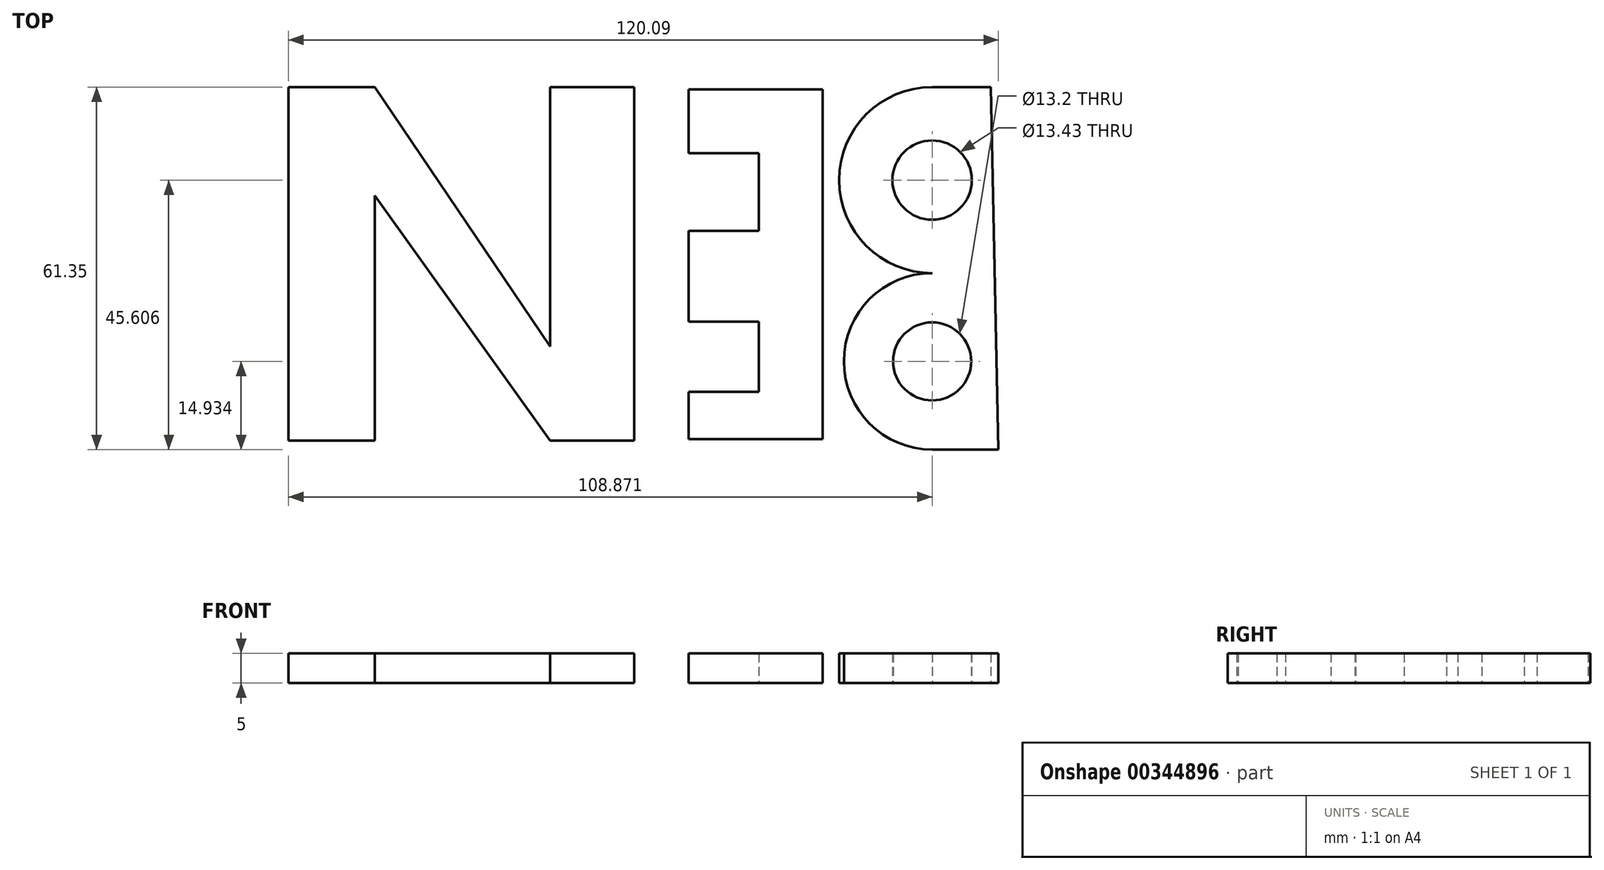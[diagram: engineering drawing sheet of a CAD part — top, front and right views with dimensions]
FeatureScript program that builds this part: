
annotation { "Feature Type Name" : "Feature", "Feature Type Description" : "" }
export const myFeature = defineFeature(function(context is Context, id is Id, definition is map)
    precondition{}
    {
        {
            var Q0;
            Q0=qCreatedBy(makeId("Top.planeOp"),FACE);
            var sketch = newSketch(context, id + "F0", { "sketchPlane" : qUnion([Q0])});
            skArc(sketch, "E0", {"start": v(-12.54, 27.73) * mm, "mid": v(-28.28, 11.99) * mm, "end": v(-12.54, -3.76) * mm});
            skArc(sketch, "E1", {"start": v(-12.54, -3.76) * mm, "mid": v(-27.47, -18.69) * mm, "end": v(-12.54, -33.62) * mm});
            skLineSegment(sketch, "E2", {"start": v(-12.54, 27.73) * mm, "end": v(-2.63, 27.73) * mm});
            skLineSegment(sketch, "E3", {"start": v(-12.54, -33.62) * mm, "end": v(-1.32, -33.62) * mm});
            skLineSegment(sketch, "E4", {"start": v(-1.32, -33.62) * mm, "end": v(-2.63, 27.73) * mm});
            skPoint(sketch, "E5.orphan", {"position": v(-1.32, 27.73) * mm});
            skCircle(sketch, "E6", {"center": v(-12.54, -18.69) * mm, "radius": 6.6 * mm});
            skCircle(sketch, "E7", {"center": v(-12.54, 11.99) * mm, "radius": 6.71 * mm});
            skLineSegment(sketch, "E8.bottom", {"start": v(-53.73, 27.33) * mm, "end": v(-31.07, 27.33) * mm});
            skLineSegment(sketch, "E8.top", {"start": v(-53.73, -31.82) * mm, "end": v(-31.07, -31.82) * mm});
            skLineSegment(sketch, "E8.left", {"start": v(-53.73, 27.33) * mm, "end": v(-53.73, 16.53) * mm});
            skLineSegment(sketch, "E8.right", {"start": v(-31.07, 27.33) * mm, "end": v(-31.07, -31.82) * mm});
            skLineSegment(sketch, "E9.bottom", {"start": v(-53.73, 16.53) * mm, "end": v(-41.86, 16.53) * mm});
            skLineSegment(sketch, "E9.top", {"start": v(-53.73, 3.37) * mm, "end": v(-41.86, 3.37) * mm});
            skLineSegment(sketch, "E9.right", {"start": v(-41.86, 16.53) * mm, "end": v(-41.86, 3.37) * mm});
            skLineSegment(sketch, "E10.bottom", {"start": v(-53.73, -11.96) * mm, "end": v(-41.86, -11.96) * mm});
            skLineSegment(sketch, "E10.top", {"start": v(-53.73, -23.83) * mm, "end": v(-41.86, -23.83) * mm});
            skLineSegment(sketch, "E10.right", {"start": v(-41.86, -11.96) * mm, "end": v(-41.86, -23.83) * mm});
            skLineSegment(sketch, "E11.trimOffspring", {"start": v(-53.73, 3.37) * mm, "end": v(-53.73, -11.96) * mm});
            skLineSegment(sketch, "E12.trimOffspring", {"start": v(-53.73, -23.83) * mm, "end": v(-53.73, -31.82) * mm});
            skLineSegment(sketch, "E13.bottom", {"start": v(-62.93, -32.08) * mm, "end": v(-77.18, -32.08) * mm});
            skLineSegment(sketch, "E13.top", {"start": v(-62.93, 27.7) * mm, "end": v(-77.18, 27.7) * mm});
            skLineSegment(sketch, "E13.left", {"start": v(-62.93, -32.08) * mm, "end": v(-62.93, 27.7) * mm});
            skLineSegment(sketch, "E13.right", {"start": v(-77.18, -16.15) * mm, "end": v(-77.18, 27.7) * mm});
            skLineSegment(sketch, "E14", {"start": v(-77.18, -32.08) * mm, "end": v(-106.81, 9.38) * mm});
            skLineSegment(sketch, "E15", {"start": v(-106.81, 9.38) * mm, "end": v(-106.81, -32.08) * mm});
            skLineSegment(sketch, "E16", {"start": v(-77.18, -16.15) * mm, "end": v(-106.81, 27.7) * mm});
            skLineSegment(sketch, "E17", {"start": v(-106.81, 27.7) * mm, "end": v(-121.4, 27.7) * mm});
            skLineSegment(sketch, "E18", {"start": v(-121.4, 27.7) * mm, "end": v(-121.4, -32.08) * mm});
            skLineSegment(sketch, "E19", {"start": v(-121.4, -32.08) * mm, "end": v(-106.81, -32.08) * mm});
            skSolve(sketch);
        }
        {
            var Q0;
            Q0=makeQuery(id+"F0.imprint","IMPRINT",FACE,{"disambiguationData":[TD([[makeQuery(id+"F0.imprint","IMPRINT",EDGE,{"derivedFrom":sQuery(id+"F0.wireOp",EDGE,"E0")}),1.0]])]});
            var Q1;
            Q1=makeQuery(id+"F0.imprint","IMPRINT",FACE,{"disambiguationData":[TD([[makeQuery(id+"F0.imprint","IMPRINT",EDGE,{"derivedFrom":sQuery(id+"F0.wireOp",EDGE,"E8.bottom")}),-1.0]])]});
            var Q2;
            Q2=makeQuery(id+"F0.imprint","IMPRINT",FACE,{"disambiguationData":[TD([[makeQuery(id+"F0.imprint","IMPRINT",EDGE,{"derivedFrom":sQuery(id+"F0.wireOp",EDGE,"E13.bottom")}),-1.0]])]});
            extrude(context, id + "F1", {"entities" : qUnion([Q0, Q1, Q2]), "depth" : 5 * mm});
        }
    });
